# Revit family: KS Polar plus, DS 40, Ø108-160
name_source: partatom
category: HLS-Bauteile
revit_build: Autodesk Revit 2018 (Build: 20190510_1515(x64)
units: mm (PartAtom-declared; Revit-internal decimal feet)

## family parameters
Arbeitsebenenbasiert = Ja
Beim Laden mit Abzugskörper schneiden = Nein
Bemaßung runder Anschluss = Durchmesser verwenden
Gemeinsam genutzt = Ja
Immer vertikal = Nein
Raumberechnungspunkt = Nein
Teiletyp = Normal

## types (8) — shared parameters
A = 66 mm  [stored 0.216535 ft]
Anschluss = M10/M12
Baustoffklasse = B2
DS = 40 mm  [stored 0.131234 ft]
DVS = 18 mm  [stored 0.0590551 ft]
Dichte Kern = 145 kg/m³
Dämmkörper = AC/PU
Dämmstärke = 40 mm  [stored 0.131234 ft]
Fabrikat = MEFA
Firma = MEFA Befestigungs- und Montagesysteme GmbH
HGA = 22 mm  [stored 0.0721785 ft]
Kurztext1 = Kälteschelle Polar Plus
L = 51 mm  [stored 0.167323 ft]
MB = 35 mm  [stored 0.114829 ft]
MD = 4 mm  [stored 0.0131234 ft]
Material = Stahl
Materialname = S235
Mengeneinheit = St
Oberflaeche = galvanisch verzinkt
Rohrschellentyp = Maxima PSM
Schalenlänge = 51 mm
Vorgabe-Ansicht = 1219 mm
Wasserdampfdiffusionswiderstand = 7000 µ
Wärmeleitfähigkeit = 0.031 W/mK
max. Temperaturbeständigkeit = 105 °C
mittl. Nenndruckfestigkeit Kern = 1,9 N/mm²
stat. Belastung Kern = 0,38 N/mm²

## per-type parameters (varying)
| type | AB | Anschlußhöhe | Artikelnummer | B | Breite | D | D0 | DF1 | DF2 | Dmax | Dmin | EAN | Gewicht | Gewicht pro Bauteil | H | Kurztext2 | R | RM | Rohraußendurchmesser Kunststoff | Rohraußendurchmesser Stahl | S | max. zul. Last | vpe |
| Kälteschelle Polar plus, DS 40, M10/M12, Ø108 | 0 mm  [stored 0 ft] | 67 mm | 74641080 | 265 mm | 265 mm | 108 mm  [stored 0.354331 ft] | 188 mm | 33 mm  [stored 0.108268 ft] | 32 mm  [stored 0.104987 ft] | 112 mm  [stored 0.367454 ft] | 108 mm  [stored 0.354331 ft] | 4250928442871 | 1.06 kg | 1.06 kg | 218 mm | 108 mm Iso 40 x 51 mm M10/M12 | 94 mm  [stored 0.308399 ft] | 98 mm  [stored 0.321522 ft] |  | 108 mm | 232 mm | 1.93 kN | 10 St |
| Kälteschelle Polar plus, DS 40, M10/M12, Ø110 | 2 mm  [stored 0.00656168 ft] | 66 mm | 74641100 | 265 mm | 265 mm | 110 mm  [stored 0.360892 ft] | 190 mm | 34 mm | 33 mm  [stored 0.108268 ft] | 110 mm  [stored 0.360892 ft] | 108 mm  [stored 0.354331 ft] | 4250928442888 | 1.06 kg | 1.06 kg | 220 mm | 110 mm Iso 40 x 51 mm M10/M12 | 95 mm  [stored 0.31168 ft] | 99 mm  [stored 0.324803 ft] | 110 mm |  | 231 mm | 1.97 kN | 10 St |
| Kälteschelle Polar plus, DS 40, M10/M12, Ø114,3 | 0 mm  [stored 0 ft] | 64 mm | 74641140 | 272 mm | 265 mm | 114 mm  [stored 0.374016 ft] | 194 mm | 34 mm | 34 mm | 116 mm  [stored 0.380577 ft] | 114 mm  [stored 0.374016 ft] | 4250928442895 | 1.06 kg | 1.06 kg | 224 mm | 114,3 mm Iso 40 x 51 mm M10/M12 | 97 mm | 101 mm |  | 114,3 mm | 238 mm | 2.05 kN | 10 St |
| Kälteschelle Polar plus, DS 40, M10/M12, Ø125 | 1 mm  [stored 0.00328084 ft] | 66 mm | 74641250 | 280 mm | 278 mm | 125 mm  [stored 0.410105 ft] | 205 mm | 32 mm  [stored 0.104987 ft] | 32 mm  [stored 0.104987 ft] | 128 mm  [stored 0.419948 ft] | 124 mm  [stored 0.406824 ft] | 4250928442901 | 1.12 kg | 1.12 kg | 235 mm | 125 mm Iso 40 x 51 mm M10/M12 | 103 mm | 107 mm | 125 mm |  | 248 mm | 2.24 kN | 1 St |
| Kälteschelle Polar plus, DS 40, M10/M12, Ø133 | 2 mm  [stored 0.00656168 ft] | 66 mm | 74641330 | 287 mm | 287 mm | 133 mm  [stored 0.436352 ft] | 213 mm | 32 mm  [stored 0.104987 ft] | 32 mm  [stored 0.104987 ft] | 135 mm  [stored 0.442913 ft] | 131 mm  [stored 0.42979 ft] | 4250928442918 | 1.15 kg | 1.15 kg | 243 mm | 133 mm Iso 40 x 51 mm M10/M12 | 107 mm | 111 mm |  | 133 mm | 255 mm | 2.38 kN | 1 St |
| Kälteschelle Polar plus, DS 40, M10/M12, Ø139,7 | 1 mm  [stored 0.00328084 ft] | 67 mm | 74641400 | 297 mm | 297 mm | 140 mm  [stored 0.459318 ft] | 220 mm | 34 mm | 33 mm  [stored 0.108268 ft] | 142 mm  [stored 0.465879 ft] | 139 mm  [stored 0.456037 ft] | 4250928442925 | 1.20 kg | 1.20 kg | 250 mm | 139,7 mm Iso 40 x 51 mm M10/M12 | 110 mm  [stored 0.360892 ft] | 114 mm  [stored 0.374016 ft] |  | 139,7 mm | 263 mm | 2.50 kN | 1 St |
| Kälteschelle Polar plus, DS 40, M10/M12, Ø159 | 1 mm  [stored 0.00328084 ft] | 67 mm | 74641590 | 315 mm | 285 mm | 159 mm  [stored 0.521654 ft] | 239 mm | 34 mm | 33 mm  [stored 0.108268 ft] | 160 mm  [stored 0.524934 ft] | 158 mm | 4250928442932 | 1.28 kg | 1.28 kg | 269 mm | 159 mm Iso 40 x 51 mm M10/M12 | 120 mm  [stored 0.393701 ft] | 124 mm  [stored 0.406824 ft] |  | 159 mm | 281 mm | 2.85 kN | 1 St |
| Kälteschelle Polar plus, DS 40, M10/M12, Ø160 | 2 mm  [stored 0.00656168 ft] | 66 mm | 74641600 | 315 mm | 287 mm | 160 mm  [stored 0.524934 ft] | 240 mm | 34 mm | 33 mm  [stored 0.108268 ft] | 160 mm  [stored 0.524934 ft] | 158 mm | 4250928442949 | 1.28 kg | 1.28 kg | 270 mm | 160 mm Iso 40 x 51 mm M10/M12 | 120 mm  [stored 0.393701 ft] | 124 mm  [stored 0.406824 ft] | 160 mm |  | 281 mm | 2.87 kN | 1 St |

note: [stored X ft] marks values corroborated as IEEE doubles in the binary element streams (Revit-internal decimal feet)

## geometry (parser evidence)
native form markers: Sweep x5
no freeform markers — native parametric forms only
